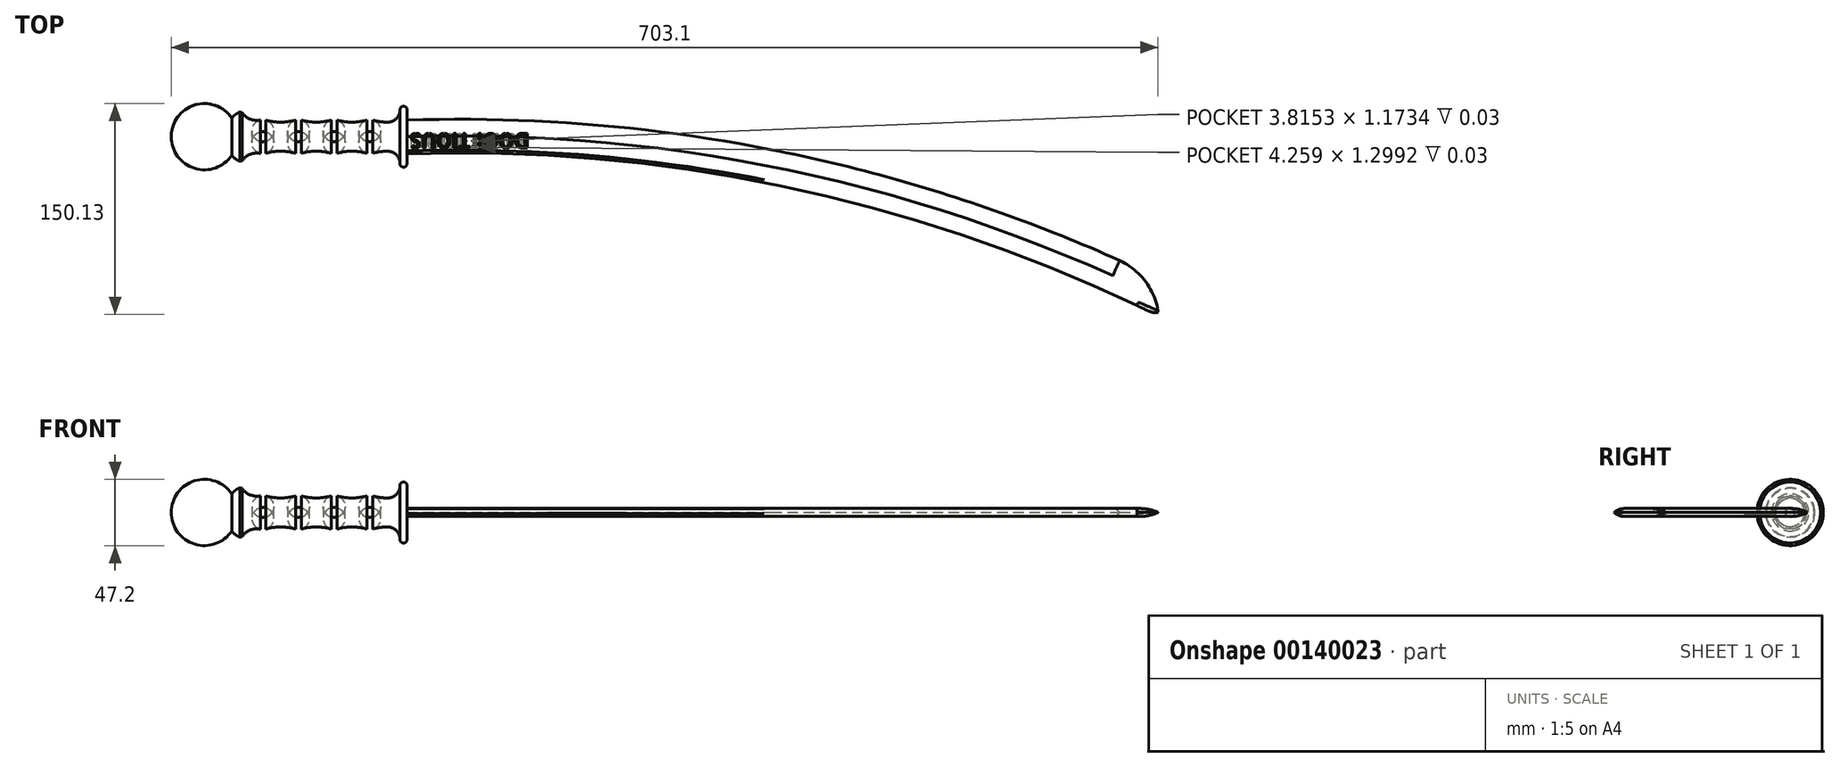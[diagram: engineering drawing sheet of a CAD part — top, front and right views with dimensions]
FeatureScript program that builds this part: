
annotation { "Feature Type Name" : "Feature", "Feature Type Description" : "" }
export const myFeature = defineFeature(function(context is Context, id is Id, definition is map)
    precondition{}
    {
        {
            var Q0;
            Q0=qCreatedBy(makeId("Top.planeOp"),FACE);
            var sketch = newSketch(context, id + "F0", { "sketchPlane" : qUnion([Q0])});
            skLineSegment(sketch, "E0", {"start": v(0, 0) * mm, "end": v(-168.04, 0) * mm});
            skLineSegment(sketch, "E1", {"start": v(-168.04, 0) * mm, "end": v(-168.04, -23.06) * mm, "construction": true});
            skLineSegment(sketch, "E2", {"start": v(0, 0) * mm, "end": v(0, 19.16) * mm});
            skArc(sketch, "E3", {"start": v(0, 19.16) * mm, "mid": v(-2.54, 21.7) * mm, "end": v(-5.08, 19.16) * mm});
            skArc(sketch, "E4", {"start": v(-13.92, 10.33) * mm, "mid": v(-7.67, 12.92) * mm, "end": v(-5.08, 19.16) * mm});
            skLineSegment(sketch, "E5", {"start": v(-13.92, 19.16) * mm, "end": v(-13.92, 10.33) * mm, "construction": true});
            skArc(sketch, "E6", {"start": v(-24.5, 11.8) * mm, "mid": v(-19.26, 10.7) * mm, "end": v(-13.92, 10.33) * mm});
            skArc(sketch, "E7", {"start": v(-24.5, 11.8) * mm, "mid": v(-26.62, 12.09) * mm, "end": v(-28.74, 11.8) * mm});
            skLineSegment(sketch, "E8", {"start": v(-26.62, 4.28) * mm, "end": v(-26.62, 12.09) * mm, "construction": true});
            skLineSegment(sketch, "E9", {"start": v(-28.74, 11.8) * mm, "end": v(-24.5, 11.8) * mm, "construction": true});
            skArc(sketch, "E10.MirrorCS", {"start": v(-28.74, 11.8) * mm, "mid": v(-33.98, 10.7) * mm, "end": v(-39.32, 10.33) * mm});
            skArc(sketch, "E11.1.0.0", {"start": v(-49.9, 11.8) * mm, "mid": v(-44.66, 10.7) * mm, "end": v(-39.32, 10.33) * mm});
            skArc(sketch, "E11.1.0.1", {"start": v(-49.9, 11.8) * mm, "mid": v(-52.02, 12.09) * mm, "end": v(-54.14, 11.8) * mm});
            skArc(sketch, "E11.1.0.2", {"start": v(-54.14, 11.8) * mm, "mid": v(-59.38, 10.7) * mm, "end": v(-64.72, 10.33) * mm});
            skArc(sketch, "E11.2.0.0", {"start": v(-75.3, 11.8) * mm, "mid": v(-70.06, 10.7) * mm, "end": v(-64.72, 10.33) * mm});
            skArc(sketch, "E11.2.0.1", {"start": v(-75.3, 11.8) * mm, "mid": v(-77.42, 12.09) * mm, "end": v(-79.54, 11.8) * mm});
            skArc(sketch, "E11.2.0.2", {"start": v(-79.54, 11.8) * mm, "mid": v(-84.78, 10.7) * mm, "end": v(-90.12, 10.33) * mm});
            skArc(sketch, "E11.3.0.0", {"start": v(-100.7, 11.8) * mm, "mid": v(-95.46, 10.7) * mm, "end": v(-90.12, 10.33) * mm});
            skArc(sketch, "E11.3.0.1", {"start": v(-100.7, 11.8) * mm, "mid": v(-102.82, 12.09) * mm, "end": v(-104.94, 11.8) * mm});
            skArc(sketch, "E11.3.0.2", {"start": v(-104.94, 11.8) * mm, "mid": v(-110.18, 10.7) * mm, "end": v(-115.52, 10.33) * mm});
            skLineSegment(sketch, "E11.direction1", {"start": v(-24.5, 11.8) * mm, "end": v(-49.9, 11.8) * mm, "construction": true});
            skArc(sketch, "E12", {"start": v(-124.92, 13.25) * mm, "mid": v(-151.38, 22.56) * mm, "end": v(-168.04, 0) * mm});
            skArc(sketch, "E13", {"start": v(-118.05, 17.9) * mm, "mid": v(-121.88, 16.15) * mm, "end": v(-124.92, 13.25) * mm});
            skArc(sketch, "E14", {"start": v(-118.05, 17.9) * mm, "mid": v(-116.97, 14.05) * mm, "end": v(-115.52, 10.33) * mm});
            skSolve(sketch);
        }
        {
            var Q0;
            Q0=makeQuery(id+"F0.imprint","IMPRINT",FACE,{"disambiguationData":[TD([[makeQuery(id+"F0.imprint","IMPRINT",EDGE,{"derivedFrom":sQuery(id+"F0.wireOp",EDGE,"E0")}),-1.0]])]});
            var Q1;
            Q1 = qConstructionFilter(qBodyType(qCreatedBy(id + "F0" ,EDGE), BodyType.WIRE), ConstructionObject.NO);
            var Q2;
            Q2=sQuery(id+"F0.wireOp",EDGE,"E0");
            revolve(context, id + "F1", {"entities" : qUnion([Q0]), "surfaceEntities" : qUnion([Q1]), "axis" : qUnion([Q2]), "revolveType" : RevolveType.FULL});
        }
        {
            var Q0;
            Q0=makeQuery(id+"F1.opRevolve","SWEPT_EDGE",EDGE,{"disambiguationData":[OSD([sQuery(id+"F0.wireOp",EDGE,"E11.3.0.2"),sQuery(id+"F0.wireOp",EDGE,"E14")])]});
            fillet(context, id + "F2", {"entities" : qUnion([Q0]), "radius" : 12.7 * mm, "tangentPropagation" : true, "allowEdgeOverflow" : false});
        }
        {
            var Q0;
            Q0=makeQuery(id+"F2.opFillet","BLEND_EDGE",EDGE,{"blendedFrom":[makeQuery(id+"F1.opRevolve","SWEPT_EDGE",EDGE,{"disambiguationData":[OSD([sQuery(id+"F0.wireOp",EDGE,"E11.3.0.2"),sQuery(id+"F0.wireOp",EDGE,"E14")])]}),makeQuery(id+"F1.opRevolve","SWEPT_FACE",FACE,{"disambiguationData":[OSD([sQuery(id+"F0.wireOp",EDGE,"E13")])]})],"blendedInto":[makeQuery(id+"F1.opRevolve","SWEPT_FACE",FACE,{"disambiguationData":[OSD([sQuery(id+"F0.wireOp",EDGE,"E13")])]})]});
            chamfer(context, id + "F3", {"entities" : qUnion([Q0]), "width" : 1.27 * mm, "tangentPropagation" : true});
        }
        {
            var Q0;
            Q0=qCreatedBy(makeId("Top.planeOp"),FACE);
            var sketch = newSketch(context, id + "F4", { "sketchPlane" : qUnion([Q0])});
            skArc(sketch, "E15", {"start": v(502.82, -98.95) * mm, "mid": v(257.05, -20.81) * mm, "end": v(0, 0) * mm, "construction": true});
            skArc(sketch, "E16.0", {"start": v(507.67, -88.14) * mm, "mid": v(259.53, -9.22) * mm, "end": v(0, 11.85) * mm});
            skArc(sketch, "E17.0", {"start": v(535.55, -127.76) * mm, "mid": v(274.91, -36.9) * mm, "end": v(0, -12.15) * mm});
            skLineSegment(sketch, "E18", {"start": v(0, 11.85) * mm, "end": v(0, -12.15) * mm});
            skArc(sketch, "E19", {"start": v(535.55, -127.76) * mm, "mid": v(526.9, -104.22) * mm, "end": v(507.67, -88.14) * mm});
            skSolve(sketch);
        }
        {
            var Q0;
            Q0=makeQuery(id+"F4.imprint","IMPRINT",FACE,{"disambiguationData":[TD([[makeQuery(id+"F4.imprint","IMPRINT",EDGE,{"derivedFrom":sQuery(id+"F4.wireOp",EDGE,"E16.0")}),1.0]])]});
            extrude(context, id + "F5", {"entities" : qUnion([Q0]), "operationType" : NewBodyOperationType.ADD, "endBound" : BoundingType.SYMMETRIC, "depth" : 5.7 * mm});
        }
        {
            var Q0;
            Q0=makeQuery(id+"F1.opRevolve","SWEPT_FACE",FACE,{"disambiguationData":[OSD([sQuery(id+"F0.wireOp",EDGE,"E2")])]});
            var sketch = newSketch(context, id + "F6", { "sketchPlane" : qUnion([Q0])});
            skLineSegment(sketch, "E20", {"start": v(0, 0) * mm, "end": v(11.85, 0) * mm, "construction": true});
            skLineSegment(sketch, "E21", {"start": v(0, 0) * mm, "end": v(0, -2.86) * mm, "construction": true});
            skLineSegment(sketch, "E22", {"start": v(0, -2.86) * mm, "end": v(-11.32, -2.86) * mm, "construction": true});
            skArc(sketch, "E23", {"start": v(0, -2.86) * mm, "mid": v(6.1, -2.13) * mm, "end": v(11.85, 0) * mm});
            skLineSegment(sketch, "E24", {"start": v(0, -2.86) * mm, "end": v(0, -8.2) * mm});
            skLineSegment(sketch, "E25", {"start": v(0, -8.2) * mm, "end": v(14.4, -8.2) * mm});
            skLineSegment(sketch, "E26", {"start": v(14.4, -8.2) * mm, "end": v(14.4, 0) * mm});
            skArc(sketch, "E27.MirrorCS", {"start": v(0, 2.86) * mm, "mid": v(6.1, 2.13) * mm, "end": v(11.85, 0) * mm});
            skLineSegment(sketch, "E28.MirrorCS", {"start": v(14.4, 8.2) * mm, "end": v(14.4, 0) * mm});
            skLineSegment(sketch, "E29.MirrorCS", {"start": v(0, 2.86) * mm, "end": v(0, 8.2) * mm});
            skLineSegment(sketch, "E30.MirrorCS", {"start": v(0, 8.2) * mm, "end": v(14.4, 8.2) * mm});
            skSolve(sketch);
        }
        {
            var Q0;
            Q0 = qSketchRegion(id + "F6", true);
            var Q1;
            Q1=makeQuery(id+"F5.opExtrude","CAP_EDGE",EDGE,{"disambiguationData":[OSD([sQuery(id+"F4.wireOp",EDGE,"E16.0")])],"isStart":true});
            var Q2;
            Q2=makeQuery(id+"F5.opExtrude","CAP_EDGE",EDGE,{"disambiguationData":[OSD([sQuery(id+"F4.wireOp",EDGE,"E19")])],"isStart":true});
            sweep(context, id + "F7", {"operationType" : NewBodyOperationType.REMOVE, "profiles" : qUnion([Q0]), "path" : qUnion([Q1, Q2])});
        }
        {
            var Q0;
            Q0=makeQuery(id+"F5.opExtrude","CAP_EDGE",EDGE,{"disambiguationData":[OSD([sQuery(id+"F4.wireOp",EDGE,"E17.0")])],"isStart":false});
            var Q1;
            Q1=makeQuery(id+"F5.opExtrude","CAP_EDGE",EDGE,{"disambiguationData":[OSD([sQuery(id+"F4.wireOp",EDGE,"E17.0")])],"isStart":true});
            fillet(context, id + "F8", {"entities" : qUnion([Q0, Q1]), "radius" : 2.54 * mm, "tangentPropagation" : true, "allowEdgeOverflow" : false});
        }
        {
            var Q0;
            Q0=makeQuery(id+"F5.opExtrude","CAP_FACE",FACE,{"disambiguationData":[OSD([sQuery(id+"F4.wireOp",EDGE,"E16.0"),sQuery(id+"F4.wireOp",EDGE,"E17.0"),sQuery(id+"F4.wireOp",EDGE,"E18"),sQuery(id+"F4.wireOp",EDGE,"E19")])],"isStart":false});
            var sketch = newSketch(context, id + "F9", { "sketchPlane" : qUnion([Q0])});
            skText(sketch, "E31", { "text": "DOOFTIOUS", "fontName": "AllertaStencil-Regular.ttf"});
            const initialGuessF9  = {"E31": [0.08697, 0.00241, -1, 0, 0.01054]};
            skSetInitialGuess(sketch, initialGuessF9);
            skSolve(sketch);
        }
        {
            var Q0;
            Q0 = qSketchRegion(id + "F9", true);
            extrude(context, id + "F10", {"entities" : qUnion([Q0]), "oppositeDirection" : true, "depth" : 2.13 * mm, "hasSecondDirection" : true, "secondDirectionOppositeDirection" : false, "secondDirectionDepth" : 25.4 * mm});
        }
        {
            var Q0;
            Q0=makeQuery(id+"F10.opExtrude","CAP_FACE",FACE,{"disambiguationData":[OSD([sQuery(id+"F9.wireOp",EDGE,"E31.sketch_text.stroke-219"),sQuery(id+"F9.wireOp",EDGE,"E31.sketch_text.stroke-220"),sQuery(id+"F9.wireOp",EDGE,"E31.sketch_text.stroke-221"),sQuery(id+"F9.wireOp",EDGE,"E31.sketch_text.stroke-222"),sQuery(id+"F9.wireOp",EDGE,"E31.sketch_text.stroke-223"),sQuery(id+"F9.wireOp",EDGE,"E31.sketch_text.stroke-224"),sQuery(id+"F9.wireOp",EDGE,"E31.sketch_text.stroke-225"),sQuery(id+"F9.wireOp",EDGE,"E31.sketch_text.stroke-226"),sQuery(id+"F9.wireOp",EDGE,"E31.sketch_text.stroke-227"),sQuery(id+"F9.wireOp",EDGE,"E31.sketch_text.stroke-228"),sQuery(id+"F9.wireOp",EDGE,"E31.sketch_text.stroke-229"),sQuery(id+"F9.wireOp",EDGE,"E31.sketch_text.stroke-230"),sQuery(id+"F9.wireOp",EDGE,"E31.sketch_text.stroke-231")])],"isStart":true});
            var sketch = newSketch(context, id + "F11", { "sketchPlane" : qUnion([Q0])});
            skLineSegment(sketch, "E32.bottom", {"start": v(91.03, -15.78) * mm, "end": v(-6.45, -15.78) * mm});
            skLineSegment(sketch, "E32.top", {"start": v(91.03, 6.68) * mm, "end": v(-6.45, 6.68) * mm});
            skLineSegment(sketch, "E32.left", {"start": v(91.03, -15.78) * mm, "end": v(91.03, 6.68) * mm});
            skLineSegment(sketch, "E32.right", {"start": v(-6.45, -15.78) * mm, "end": v(-6.45, 6.68) * mm});
            skSolve(sketch);
        }
        {
            var Q0;
            Q0=makeQuery(id+"F11.imprint","IMPRINT",FACE,{"disambiguationData":[TD([[makeQuery(id+"F11.imprint","IMPRINT",EDGE,{"derivedFrom":sQuery(id+"F11.wireOp",EDGE,"E32.bottom")}),-1.0]])]});
            extrude(context, id + "F12", {"entities" : qUnion([Q0]), "operationType" : NewBodyOperationType.ADD, "oppositeDirection" : true, "depth" : 3.32 * mm});
        }
        {
            var Q0;
            Q0=qCreatedBy(makeId("Top.planeOp"),FACE);
            var sketch = newSketch(context, id + "F13", { "sketchPlane" : qUnion([Q0])});
            skLineSegment(sketch, "E33.0", {"start": v(44.44, 2.41) * mm, "end": v(44.44, -8.13) * mm, "construction": true});
            skSolve(sketch);
        }
        {
            var Q0;
            Q0=makeQuery(id+"F10.opExtrude","SWEPT_BODY",BODY,{"disambiguationData":[OSD([sQuery(id+"F9.wireOp",EDGE,"E31.sketch_text.stroke-0"),sQuery(id+"F9.wireOp",EDGE,"E31.sketch_text.stroke-1"),sQuery(id+"F9.wireOp",EDGE,"E31.sketch_text.stroke-2"),sQuery(id+"F9.wireOp",EDGE,"E31.sketch_text.stroke-3")])]});
            var Q1;
            Q1=sQuery(id+"F13.wireOp",EDGE,"E33.0");
            circularPattern(context, id + "F14", {"entities" : qUnion([Q0]), "axis" : qUnion([Q1]), "angle" : 180 * degree, "instanceCount" : 2});
        }
        {
            var Q0;
            Q0=makeQuery(id+"F14.opPattern","COPY",BODY,{"derivedFrom":makeQuery(id+"F10.opExtrude","SWEPT_BODY",BODY,{"disambiguationData":[OSD([sQuery(id+"F9.wireOp",EDGE,"E31.sketch_text.stroke-0"),sQuery(id+"F9.wireOp",EDGE,"E31.sketch_text.stroke-1"),sQuery(id+"F9.wireOp",EDGE,"E31.sketch_text.stroke-2"),sQuery(id+"F9.wireOp",EDGE,"E31.sketch_text.stroke-3")])]}),"instanceName":"1"});
            var Q1;
            Q1=makeQuery(id+"F10.opExtrude","SWEPT_BODY",BODY,{"disambiguationData":[OSD([sQuery(id+"F9.wireOp",EDGE,"E31.sketch_text.stroke-0"),sQuery(id+"F9.wireOp",EDGE,"E31.sketch_text.stroke-1"),sQuery(id+"F9.wireOp",EDGE,"E31.sketch_text.stroke-2"),sQuery(id+"F9.wireOp",EDGE,"E31.sketch_text.stroke-3")])]});
            var Q2;
            Q2=makeQuery(id+"F1.opRevolve","SWEPT_BODY",BODY,{"disambiguationData":[OSD([sQuery(id+"F0.wireOp",EDGE,"E0"),sQuery(id+"F0.wireOp",EDGE,"E2"),sQuery(id+"F0.wireOp",EDGE,"E3"),sQuery(id+"F0.wireOp",EDGE,"E4"),sQuery(id+"F0.wireOp",EDGE,"E6"),sQuery(id+"F0.wireOp",EDGE,"E7"),sQuery(id+"F0.wireOp",EDGE,"E10.MirrorCS"),sQuery(id+"F0.wireOp",EDGE,"E11.1.0.0"),sQuery(id+"F0.wireOp",EDGE,"E11.1.0.1"),sQuery(id+"F0.wireOp",EDGE,"E11.1.0.2"),sQuery(id+"F0.wireOp",EDGE,"E11.2.0.0"),sQuery(id+"F0.wireOp",EDGE,"E11.2.0.1"),sQuery(id+"F0.wireOp",EDGE,"E11.2.0.2"),sQuery(id+"F0.wireOp",EDGE,"E11.3.0.0"),sQuery(id+"F0.wireOp",EDGE,"E11.3.0.1"),sQuery(id+"F0.wireOp",EDGE,"E11.3.0.2"),sQuery(id+"F0.wireOp",EDGE,"E12"),sQuery(id+"F0.wireOp",EDGE,"E13"),sQuery(id+"F0.wireOp",EDGE,"E14")])]});
            booleanBodies(context, id + "F15", {"operationType" : BooleanOperationType.SUBTRACTION, "tools" : qUnion([Q0, Q1]), "targets" : qUnion([Q2])});
        }
        {
            var Q0;
            Q0=makeQuery(id+"F7.boolean.opBoolean","MERGE",FACE,{"derivedFrom":[makeQuery(id+"F1.opRevolve","SWEPT_FACE",FACE,{"disambiguationData":[OSD([sQuery(id+"F0.wireOp",EDGE,"E2")])]}),makeQuery(id+"F7.opSweep","CAP_FACE",FACE,{"disambiguationData":[OSD([sQuery(id+"F4.wireOp",EDGE,"E16.0"),sQuery(id+"F4.wireOp",EDGE,"E18"),sQuery(id+"F6.wireOp",EDGE,"E23"),sQuery(id+"F6.wireOp",EDGE,"E24"),sQuery(id+"F6.wireOp",EDGE,"E25"),sQuery(id+"F6.wireOp",EDGE,"E26"),sQuery(id+"F6.wireOp",EDGE,"E27.MirrorCS"),sQuery(id+"F6.wireOp",EDGE,"E28.MirrorCS"),sQuery(id+"F6.wireOp",EDGE,"E29.MirrorCS"),sQuery(id+"F6.wireOp",EDGE,"E30.MirrorCS")])],"isStart":true})]});
            var sketch = newSketch(context, id + "F16", { "sketchPlane" : qUnion([Q0])});
            skArc(sketch, "E34.0", {"start": v(11.79, 0) * mm, "mid": v(6.06, -2.1) * mm, "end": v(0, -2.83) * mm});
            skArc(sketch, "E34.1", {"start": v(0, 2.83) * mm, "mid": v(6.06, 2.1) * mm, "end": v(11.79, 0) * mm});
            skFitSpline(sketch, "E34.2", {"points": [v(-9.6, -2.83) * mm, v(-9.77, -2.83) * mm, v(-10.1, -2.8) * mm, v(-10.57, -2.65) * mm, v(-11, -2.42) * mm, v(-11.4, -2.1) * mm, v(-11.65, -1.79) * mm, v(-11.82, -1.5) * mm, v(-12.03, -1.06) * mm, v(-12.12, -0.65) * mm, v(-12.12, -0.32) * mm]});
            skLineSegment(sketch, "E34.3", {"start": v(-12.12, 0.32) * mm, "end": v(-12.12, -0.32) * mm});
            skFitSpline(sketch, "E34.4", {"points": [v(-12.12, 0.32) * mm, v(-12.12, 0.48) * mm, v(-12.09, 0.8) * mm, v(-11.94, 1.28) * mm, v(-11.7, 1.72) * mm, v(-11.4, 2.1) * mm, v(-11.08, 2.36) * mm, v(-10.8, 2.53) * mm, v(-10.35, 2.74) * mm, v(-9.94, 2.83) * mm, v(-9.6, 2.83) * mm]});
            skLineSegment(sketch, "E34.5", {"start": v(0, -2.83) * mm, "end": v(-9.6, -2.83) * mm});
            skLineSegment(sketch, "E34.6", {"start": v(0, 2.83) * mm, "end": v(-9.6, 2.83) * mm});
            skSolve(sketch);
        }
        {
            var Q0;
            Q0 = qSketchRegion(id + "F16", true);
            var Q1;
            {var subQ0=sQuery(id+"F6.wireOp",EDGE,"E23");var subQ1=sQuery(id+"F4.wireOp",EDGE,"E16.0");var subQ2=sQuery(id+"F6.wireOp",EDGE,"E27.MirrorCS");var subQ3=sQuery(id+"F4.wireOp",EDGE,"E18");Q1=makeQuery(id+"F7.boolean.opBoolean","COPY",EDGE,{"disambiguationData":[TD([makeQuery(id+"F1.opRevolve","SWEPT_FACE",FACE,{"disambiguationData":[OSD([sQuery(id+"F0.wireOp",EDGE,"E2")])]}),makeQuery(id+"F7.opSweep","SWEPT_FACE",FACE,{"disambiguationData":[OSD([subQ1,subQ0])]}),makeQuery(id+"F7.opSweep","SWEPT_FACE",FACE,{"disambiguationData":[OSD([subQ1,subQ2])]}),makeQuery(id+"F7.opSweep","CAP_FACE",FACE,{"disambiguationData":[OSD([subQ1,subQ3,subQ0,sQuery(id+"F6.wireOp",EDGE,"E24"),sQuery(id+"F6.wireOp",EDGE,"E25"),sQuery(id+"F6.wireOp",EDGE,"E26"),subQ2,sQuery(id+"F6.wireOp",EDGE,"E28.MirrorCS"),sQuery(id+"F6.wireOp",EDGE,"E29.MirrorCS"),sQuery(id+"F6.wireOp",EDGE,"E30.MirrorCS")])],"isStart":true})])],"derivedFrom":makeQuery(id+"F7.opSweep","SWEPT_EDGE",EDGE,{"disambiguationData":[OSD([subQ1,subQ3,subQ0,subQ2])]})});}
            sweep(context, id + "F17", {"operationType" : NewBodyOperationType.ADD, "profiles" : qUnion([Q0]), "path" : qUnion([Q1])});
        }
    });
